# Revit family: Haworth_Planes_CollaborativeTable_HalfRound_AP_PRELIMINARY
name_source: partatom
category: Furniture
units: mm (PartAtom-declared; Revit-internal decimal feet)

## family parameters
Always vertical = Yes
Cut with Voids When Loaded = No
OmniClass Number = 23.40.70.14.64.21
OmniClass Title = Systems Furniture
Room Calculation Point = No
Shared = No
Work Plane-Based = No

## types (1)
- 1800w x 900d
    Actual Depth = 900 mm  [stored 2.95276 ft]
    Actual Height = 740 mm  [stored 2.42782 ft]
    Actual Width = 1800 mm  [stored 5.90551 ft]
    Assembly Code = E2020200
    Caster Finish = Haworth _ Polymer _ Black
    Casters = Yes
    Description = Haworth - Planes - Collaborative Table - Half Round
    Flip Top = Yes
    Flip Top Finish = Haworth _ Paint _ Undecided _ Table
    Glides = No
    Leg Height = 715 mm  [stored 2.3458 ft]
    Manufacturer = Haworth
    Model = WOPLTAF
    Revision Number = 1
    Size = Verify Final Dim. w/ Haworth
    Trim Finish = Haworth _ Polymer _ Undecided
    URL = https://www.haworth.com
    URL - Product = https://www.haworth.com
    Warranty = http://www.haworth.com

note: [stored X ft] marks values corroborated as IEEE doubles in the binary element streams (Revit-internal decimal feet)

## geometry (parser evidence)
native form markers: Sweep x13
no freeform markers — native parametric forms only
